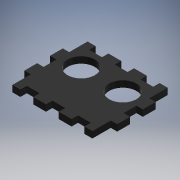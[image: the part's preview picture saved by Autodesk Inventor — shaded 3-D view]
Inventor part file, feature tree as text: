
AUTODESK INVENTOR PART (.ipt)
format: ipt  version: 2019 (Build 230136000, 136)  size: 206,336 bytes
history: native  units: mm
features: extrude x2, sketch x2
ambient origin geometry x8: Origin, YZ Plane, XZ Plane, XY Plane, X Axis, Y Axis, Z Axis, Center Point
bodies: Solid1 (feature_tree)
feature tree (4):
  extrude  "Extrusion1"  Depth=47.0mm
  extrude  "Extrusion2"  Depth=16.0mm
  sketch  "Sketch1"  dims[d0=58.0mm d1=47.0mm]
  sketch  "Sketch2"  dims[d2=17.0mm d3=16.0mm d4=16.0mm d6=4.0mm d7=0.0mm d8=4.0mm d11=8.0mm d12=8.0mm d13=4.0mm d14=4.0mm d15=0.0mm d16=4.0mm d17=8.0mm d18=26.0mm]
